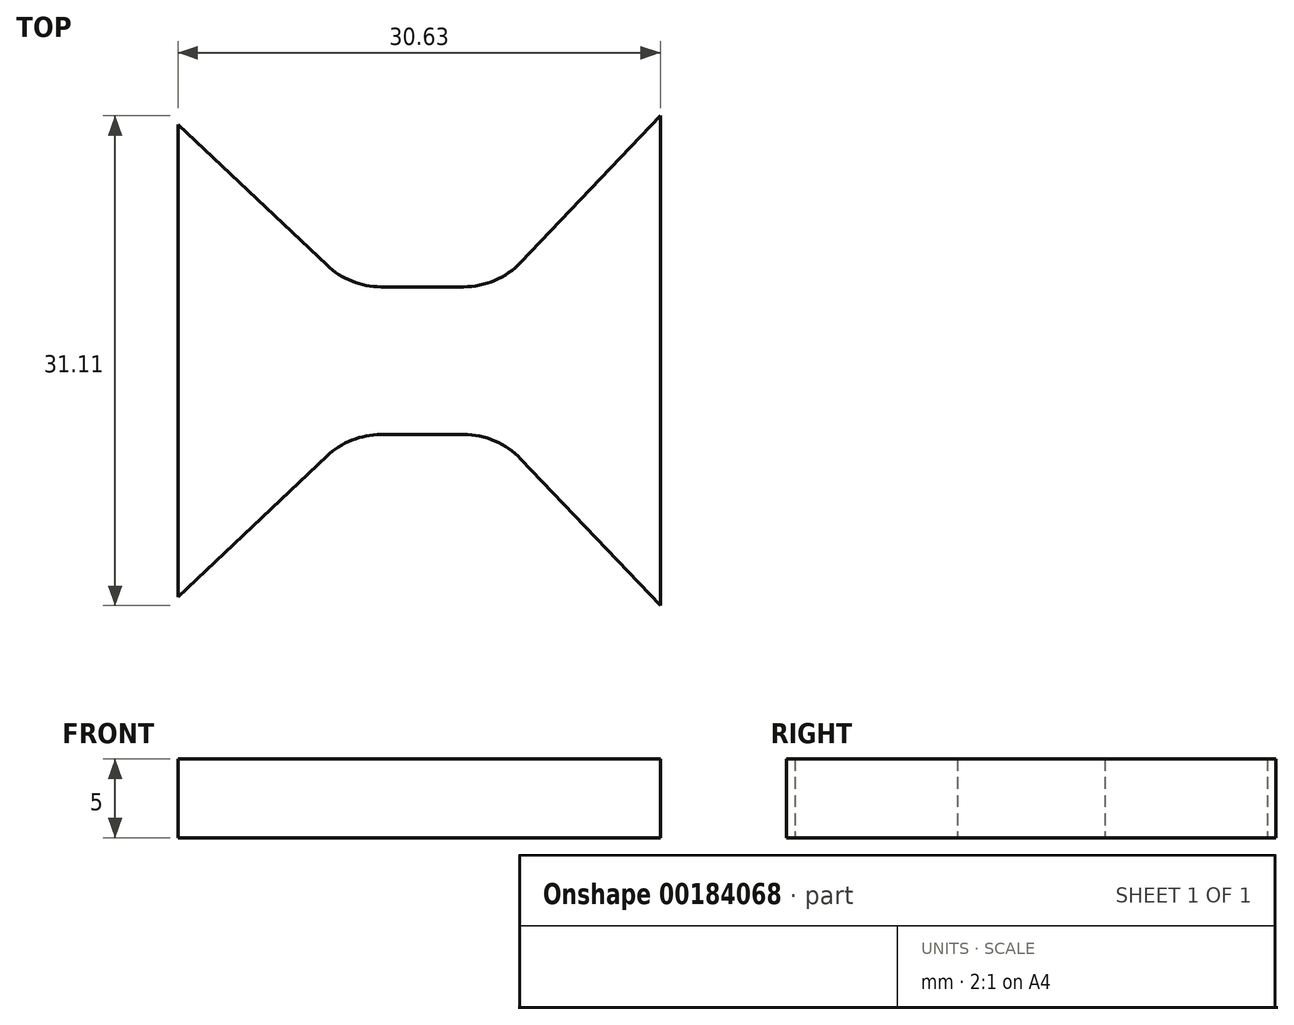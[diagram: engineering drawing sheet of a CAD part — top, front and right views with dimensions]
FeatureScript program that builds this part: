
annotation { "Feature Type Name" : "Feature", "Feature Type Description" : "" }
export const myFeature = defineFeature(function(context is Context, id is Id, definition is map)
    precondition{}
    {
        {
            var Q0;
            Q0=qCreatedBy(makeId("Top.planeOp"),FACE);
            var sketch = newSketch(context, id + "F0", { "sketchPlane" : qUnion([Q0])});
            skLineSegment(sketch, "E0", {"start": v(-19.73, 13.55) * mm, "end": v(-10.34, 13.55) * mm});
            skLineSegment(sketch, "E1", {"start": v(-19.73, 13.55) * mm, "end": v(-19.73, 4.16) * mm});
            skLineSegment(sketch, "E2", {"start": v(-19.73, 4.16) * mm, "end": v(-10.34, 4.16) * mm});
            skLineSegment(sketch, "E3", {"start": v(-10.34, 4.16) * mm, "end": v(-10.34, 13.55) * mm});
            skLineSegment(sketch, "E4", {"start": v(-10.34, 13.55) * mm, "end": v(0, 24.4) * mm});
            skLineSegment(sketch, "E5", {"start": v(0, 23.62) * mm, "end": v(0, -6.7) * mm});
            skLineSegment(sketch, "E6", {"start": v(0, -6.7) * mm, "end": v(-10.34, 4.16) * mm});
            skLineSegment(sketch, "E7", {"start": v(-19.73, 13.55) * mm, "end": v(-30.63, 23.85) * mm});
            skLineSegment(sketch, "E8", {"start": v(-30.63, 23.85) * mm, "end": v(-30.63, -6.15) * mm});
            skLineSegment(sketch, "E9", {"start": v(-30.63, -6.15) * mm, "end": v(-19.73, 4.16) * mm});
            skLineSegment(sketch, "E10", {"start": v(0, 24.4) * mm, "end": v(0, -6.7) * mm});
            skSolve(sketch);
        }
        {
            var Q0;
            Q0 = qSketchRegion(id + "F0", true);
            extrude(context, id + "F1", {"entities" : qUnion([Q0]), "depth" : 5 * mm});
        }
        {
            var Q0;
            Q0=makeQuery(id+"F1.opExtrude","SWEPT_EDGE",EDGE,{"disambiguationData":[OSD([sQuery(id+"F0.wireOp",EDGE,"E2"),sQuery(id+"F0.wireOp",EDGE,"E3"),sQuery(id+"F0.wireOp",EDGE,"E6")])]});
            var Q1;
            Q1=makeQuery(id+"F1.opExtrude","SWEPT_EDGE",EDGE,{"disambiguationData":[OSD([sQuery(id+"F0.wireOp",EDGE,"E1"),sQuery(id+"F0.wireOp",EDGE,"E2"),sQuery(id+"F0.wireOp",EDGE,"E9")])]});
            var Q2;
            Q2=makeQuery(id+"F1.opExtrude","SWEPT_EDGE",EDGE,{"disambiguationData":[OSD([sQuery(id+"F0.wireOp",EDGE,"E0"),sQuery(id+"F0.wireOp",EDGE,"E3"),sQuery(id+"F0.wireOp",EDGE,"E4")])]});
            var Q3;
            Q3=makeQuery(id+"F1.opExtrude","SWEPT_EDGE",EDGE,{"disambiguationData":[OSD([sQuery(id+"F0.wireOp",EDGE,"E0"),sQuery(id+"F0.wireOp",EDGE,"E1"),sQuery(id+"F0.wireOp",EDGE,"E7")])]});
            fillet(context, id + "F2", {"entities" : qUnion([Q0, Q1, Q2, Q3]), "radius" : 5 * mm, "tangentPropagation" : true, "allowEdgeOverflow" : false});
        }
    });
